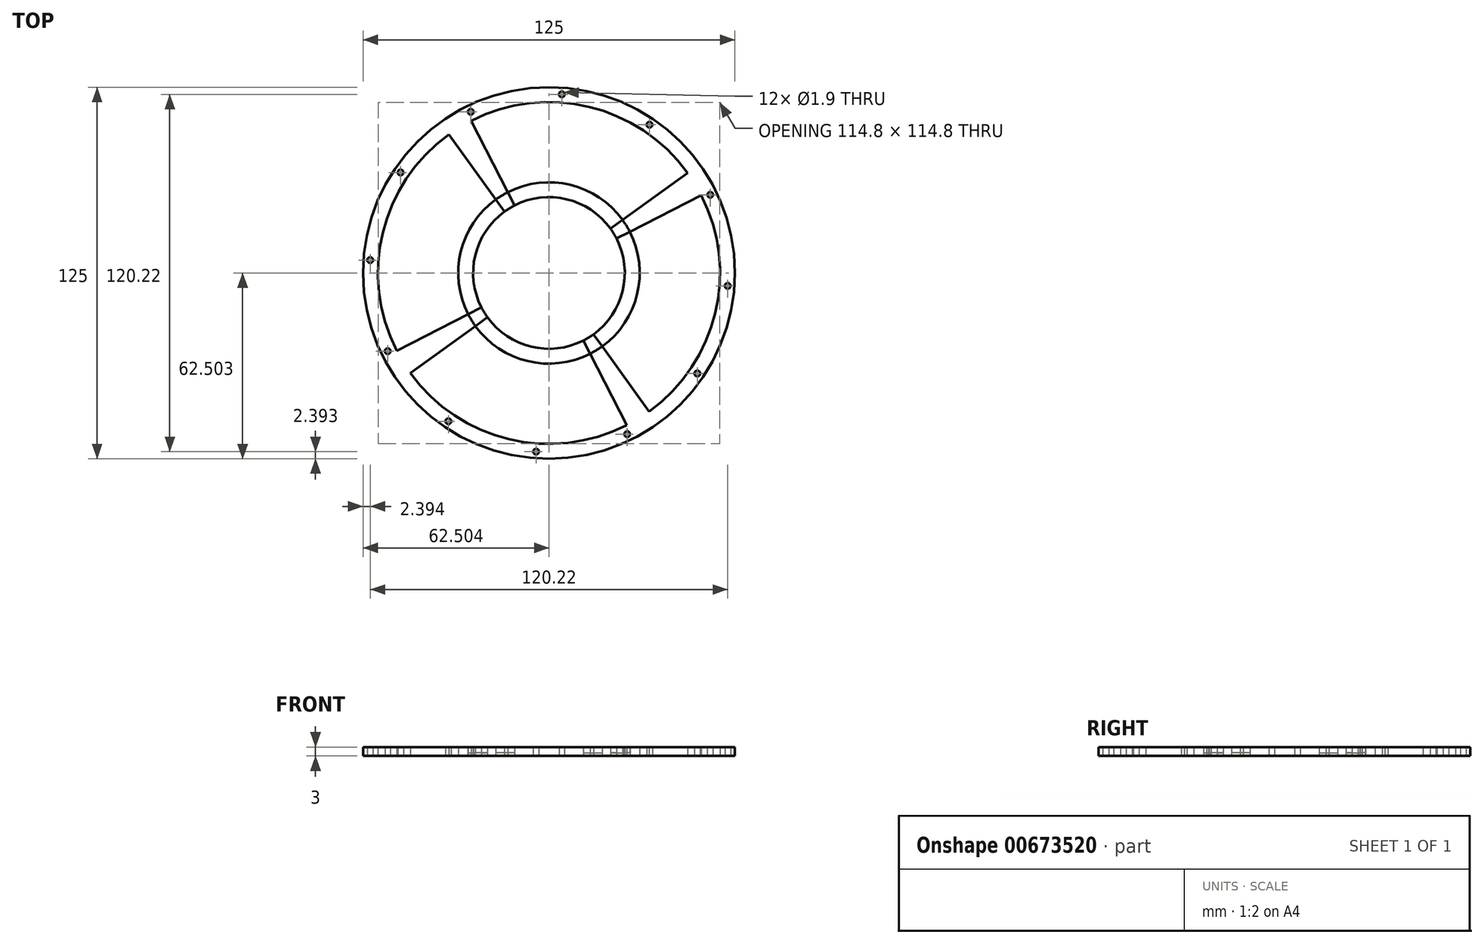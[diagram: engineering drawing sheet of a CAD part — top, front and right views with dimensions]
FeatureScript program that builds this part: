
annotation { "Feature Type Name" : "Feature", "Feature Type Description" : "" }
export const myFeature = defineFeature(function(context is Context, id is Id, definition is map)
    precondition{}
    {
        {
            var Q0;
            Q0=qCreatedBy(makeId("Top.planeOp"),FACE);
            var sketch = newSketch(context, id + "F0", { "sketchPlane" : qUnion([Q0])});
            skCircle(sketch, "E0", {"center": v(-11.5, 27.97) * mm, "radius": 25.5 * mm});
            skCircle(sketch, "E1.0", {"center": v(-11.5, 27.97) * mm, "radius": 30.5 * mm});
            skCircle(sketch, "E2", {"center": v(-11.5, 27.97) * mm, "radius": 57.5 * mm});
            skCircle(sketch, "E3.0", {"center": v(-11.5, 27.97) * mm, "radius": 62.5 * mm});
            skLineSegment(sketch, "E4", {"start": v(-11.5, 27.97) * mm, "end": v(39.71, 54.12) * mm});
            skLineSegment(sketch, "E5", {"start": v(-11.5, 27.97) * mm, "end": v(35.1, 61.67) * mm});
            skLineSegment(sketch, "E6.1.0", {"start": v(-11.5, 27.97) * mm, "end": v(-45.2, 74.57) * mm});
            skLineSegment(sketch, "E6.1.1", {"start": v(-11.5, 27.97) * mm, "end": v(-37.65, 79.18) * mm});
            skLineSegment(sketch, "E6.2.0", {"start": v(-11.5, 27.97) * mm, "end": v(-58.09, -5.72) * mm});
            skLineSegment(sketch, "E6.2.1", {"start": v(-11.5, 27.97) * mm, "end": v(-62.7, 1.82) * mm});
            skLineSegment(sketch, "E6.3.0", {"start": v(-11.5, 27.97) * mm, "end": v(22.2, -18.62) * mm});
            skLineSegment(sketch, "E6.3.1", {"start": v(-11.5, 27.97) * mm, "end": v(14.66, -23.24) * mm});
            skCircle(sketch, "E7", {"center": v(-37.8, 82.2) * mm, "radius": 0.95 * mm});
            skCircle(sketch, "E8.1.0", {"center": v(-61.39, 61.78) * mm, "radius": 0.95 * mm});
            skCircle(sketch, "E8.2.0", {"center": v(-71.6, 32.3) * mm, "radius": 0.95 * mm});
            skCircle(sketch, "E8.3.0", {"center": v(-65.72, 1.67) * mm, "radius": 0.95 * mm});
            skCircle(sketch, "E8.4.0", {"center": v(-45.3, -21.92) * mm, "radius": 0.95 * mm});
            skCircle(sketch, "E8.5.0", {"center": v(-15.83, -32.14) * mm, "radius": 0.95 * mm});
            skCircle(sketch, "E8.6.0", {"center": v(14.8, -26.25) * mm, "radius": 0.95 * mm});
            skCircle(sketch, "E8.7.0", {"center": v(38.4, -5.84) * mm, "radius": 0.95 * mm});
            skCircle(sketch, "E8.8.0", {"center": v(48.61, 23.64) * mm, "radius": 0.95 * mm});
            skCircle(sketch, "E8.9.0", {"center": v(42.73, 54.27) * mm, "radius": 0.95 * mm});
            skCircle(sketch, "E8.10.0", {"center": v(22.31, 77.86) * mm, "radius": 0.95 * mm});
            skCircle(sketch, "E8.11.0", {"center": v(-7.16, 88.08) * mm, "radius": 0.95 * mm});
            skSolve(sketch);
        }
        {
            var Q0;
            Q0 = qSketchRegion(id + "F0", true);
            var Q1;
            {var subQ0=sQuery(id+"F0.wireOp",EDGE,"E5");var subQ1=sQuery(id+"F0.wireOp",EDGE,"E0");var subQ2=makeQuery(id+"F0.imprint","INTERSECT",VERTEX,{"derivedFrom":[subQ1,subQ0]});Q1=makeQuery(id+"F0.imprint","IMPRINT",FACE,{"disambiguationData":[TD([[makeQuery(id+"F0.imprint","IMPRINT",EDGE,{"disambiguationData":[TD([[subQ2,-1.0]])],"derivedFrom":subQ1}),-1.0]])]});}
            var Q2;
            {var subQ0=sQuery(id+"F0.wireOp",EDGE,"E6.1.0");var subQ1=sQuery(id+"F0.wireOp",EDGE,"E0");var subQ2=makeQuery(id+"F0.imprint","INTERSECT",VERTEX,{"derivedFrom":[subQ1,subQ0]});Q2=makeQuery(id+"F0.imprint","IMPRINT",FACE,{"disambiguationData":[TD([[makeQuery(id+"F0.imprint","IMPRINT",EDGE,{"disambiguationData":[TD([[subQ2,-1.0]])],"derivedFrom":subQ1}),-1.0]])]});}
            var Q3;
            {var subQ0=sQuery(id+"F0.wireOp",EDGE,"E6.2.0");var subQ1=sQuery(id+"F0.wireOp",EDGE,"E0");var subQ2=makeQuery(id+"F0.imprint","INTERSECT",VERTEX,{"derivedFrom":[subQ1,subQ0]});Q3=makeQuery(id+"F0.imprint","IMPRINT",FACE,{"disambiguationData":[TD([[makeQuery(id+"F0.imprint","IMPRINT",EDGE,{"disambiguationData":[TD([[subQ2,-1.0]])],"derivedFrom":subQ1}),-1.0]])]});}
            var Q4;
            {var subQ0=sQuery(id+"F0.wireOp",EDGE,"E4");var subQ1=sQuery(id+"F0.wireOp",EDGE,"E0");var subQ2=makeQuery(id+"F0.imprint","INTERSECT",VERTEX,{"derivedFrom":[subQ1,subQ0]});Q4=makeQuery(id+"F0.imprint","IMPRINT",FACE,{"disambiguationData":[TD([[makeQuery(id+"F0.imprint","IMPRINT",EDGE,{"disambiguationData":[TD([[subQ2,1.0]])],"derivedFrom":subQ1}),-1.0]])]});}
            var Q5;
            {var subQ0=sQuery(id+"F0.wireOp",EDGE,"E5");var subQ1=sQuery(id+"F0.wireOp",EDGE,"E1.0");var subQ2=makeQuery(id+"F0.imprint","INTERSECT",VERTEX,{"derivedFrom":[subQ1,subQ0]});Q5=makeQuery(id+"F0.imprint","IMPRINT",FACE,{"disambiguationData":[TD([[makeQuery(id+"F0.imprint","IMPRINT",EDGE,{"disambiguationData":[TD([[subQ2,1.0]])],"derivedFrom":subQ1}),-1.0]])]});}
            var Q6;
            {var subQ0=sQuery(id+"F0.wireOp",EDGE,"E6.1.1");var subQ1=sQuery(id+"F0.wireOp",EDGE,"E1.0");var subQ2=makeQuery(id+"F0.imprint","INTERSECT",VERTEX,{"derivedFrom":[subQ1,subQ0]});Q6=makeQuery(id+"F0.imprint","IMPRINT",FACE,{"disambiguationData":[TD([[makeQuery(id+"F0.imprint","IMPRINT",EDGE,{"disambiguationData":[TD([[subQ2,-1.0]])],"derivedFrom":subQ1}),-1.0]])]});}
            var Q7;
            {var subQ0=sQuery(id+"F0.wireOp",EDGE,"E6.3.1");var subQ1=sQuery(id+"F0.wireOp",EDGE,"E1.0");var subQ2=makeQuery(id+"F0.imprint","INTERSECT",VERTEX,{"derivedFrom":[subQ1,subQ0]});Q7=makeQuery(id+"F0.imprint","IMPRINT",FACE,{"disambiguationData":[TD([[makeQuery(id+"F0.imprint","IMPRINT",EDGE,{"disambiguationData":[TD([[subQ2,-1.0]])],"derivedFrom":subQ1}),-1.0]])]});}
            var Q8;
            {var subQ0=sQuery(id+"F0.wireOp",EDGE,"E6.2.1");var subQ1=sQuery(id+"F0.wireOp",EDGE,"E1.0");var subQ2=makeQuery(id+"F0.imprint","INTERSECT",VERTEX,{"derivedFrom":[subQ1,subQ0]});Q8=makeQuery(id+"F0.imprint","IMPRINT",FACE,{"disambiguationData":[TD([[makeQuery(id+"F0.imprint","IMPRINT",EDGE,{"disambiguationData":[TD([[subQ2,-1.0]])],"derivedFrom":subQ1}),-1.0]])]});}
            extrude(context, id + "F1", {"entities" : qUnion([Q0, Q1, Q2, Q3, Q4, Q5, Q6, Q7, Q8]), "depth" : 3 * mm, "offsetDistance" : 25 * mm});
        }
        {
            var Q0;
            {var subQ0=sQuery(id+"F0.wireOp",EDGE,"E6.1.1");var subQ1=sQuery(id+"F0.wireOp",EDGE,"E0");var subQ2=makeQuery(id+"F0.imprint","INTERSECT",VERTEX,{"derivedFrom":[subQ1,subQ0]});Q0=makeQuery(id+"F0.imprint","IMPRINT",FACE,{"disambiguationData":[TD([[makeQuery(id+"F0.imprint","IMPRINT",EDGE,{"disambiguationData":[TD([[subQ2,-1.0]])],"derivedFrom":subQ1}),-1.0]])]});}
            var Q1;
            {var subQ0=sQuery(id+"F0.wireOp",EDGE,"E6.2.1");var subQ1=sQuery(id+"F0.wireOp",EDGE,"E0");var subQ2=makeQuery(id+"F0.imprint","INTERSECT",VERTEX,{"derivedFrom":[subQ1,subQ0]});Q1=makeQuery(id+"F0.imprint","IMPRINT",FACE,{"disambiguationData":[TD([[makeQuery(id+"F0.imprint","IMPRINT",EDGE,{"disambiguationData":[TD([[subQ2,-1.0]])],"derivedFrom":subQ1}),-1.0]])]});}
            var Q2;
            {var subQ0=sQuery(id+"F0.wireOp",EDGE,"E6.3.1");var subQ1=sQuery(id+"F0.wireOp",EDGE,"E0");var subQ2=makeQuery(id+"F0.imprint","INTERSECT",VERTEX,{"derivedFrom":[subQ1,subQ0]});Q2=makeQuery(id+"F0.imprint","IMPRINT",FACE,{"disambiguationData":[TD([[makeQuery(id+"F0.imprint","IMPRINT",EDGE,{"disambiguationData":[TD([[subQ2,-1.0]])],"derivedFrom":subQ1}),-1.0]])]});}
            var Q3;
            {var subQ0=sQuery(id+"F0.wireOp",EDGE,"E5");var subQ1=sQuery(id+"F0.wireOp",EDGE,"E0");var subQ2=makeQuery(id+"F0.imprint","INTERSECT",VERTEX,{"derivedFrom":[subQ1,subQ0]});Q3=makeQuery(id+"F0.imprint","IMPRINT",FACE,{"disambiguationData":[TD([[makeQuery(id+"F0.imprint","IMPRINT",EDGE,{"disambiguationData":[TD([[subQ2,1.0]])],"derivedFrom":subQ1}),-1.0]])]});}
            extrude(context, id + "F2", {"entities" : qUnion([Q0, Q1, Q2, Q3]), "depth" : 1 * mm, "offsetDistance" : 25 * mm});
        }
    });
